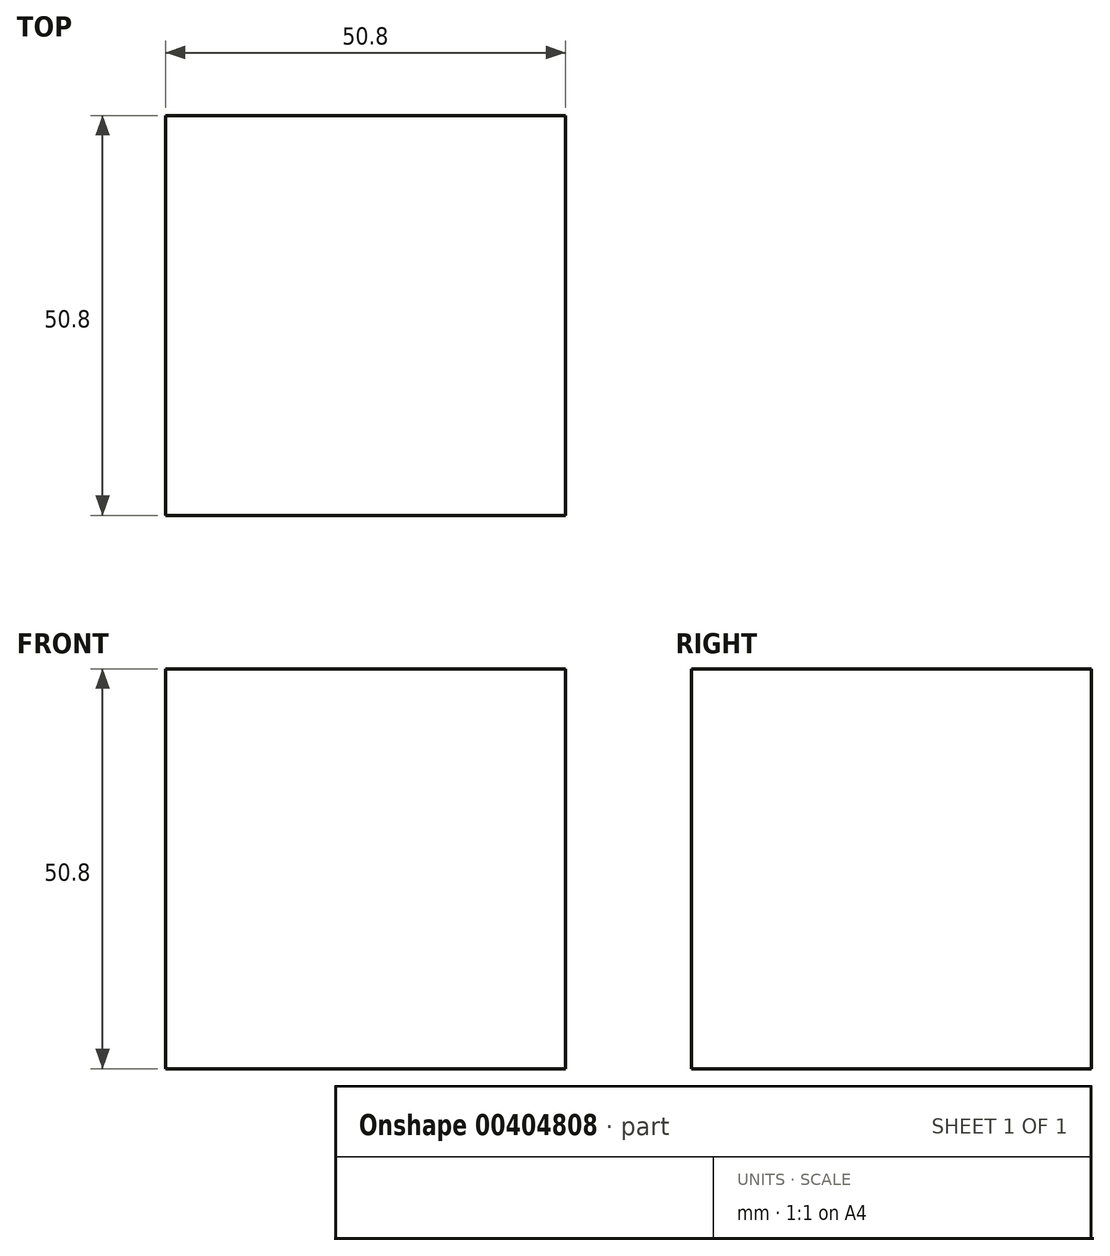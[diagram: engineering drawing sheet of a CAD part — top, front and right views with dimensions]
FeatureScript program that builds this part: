
annotation { "Feature Type Name" : "Feature", "Feature Type Description" : "" }
export const myFeature = defineFeature(function(context is Context, id is Id, definition is map)
    precondition{}
    {
        {
            var Q0;
            Q0=qCreatedBy(makeId("Top.planeOp"),FACE);
            var sketch = newSketch(context, id + "F0", { "sketchPlane" : qUnion([Q0])});
            skLineSegment(sketch, "E0.bottom", {"start": v(-25.4, 25.4) * mm, "end": v(25.4, 25.4) * mm});
            skLineSegment(sketch, "E0.top", {"start": v(-25.4, -25.4) * mm, "end": v(25.4, -25.4) * mm});
            skLineSegment(sketch, "E0.left", {"start": v(-25.4, 25.4) * mm, "end": v(-25.4, -25.4) * mm});
            skLineSegment(sketch, "E0.right", {"start": v(25.4, 25.4) * mm, "end": v(25.4, -25.4) * mm});
            skSolve(sketch);
        }
        {
            var Q0;
            Q0 = qSketchRegion(id + "F0", true);
            extrude(context, id + "F1", {"entities" : qUnion([Q0]), "depth" : 50.8 * mm});
        }
    });
